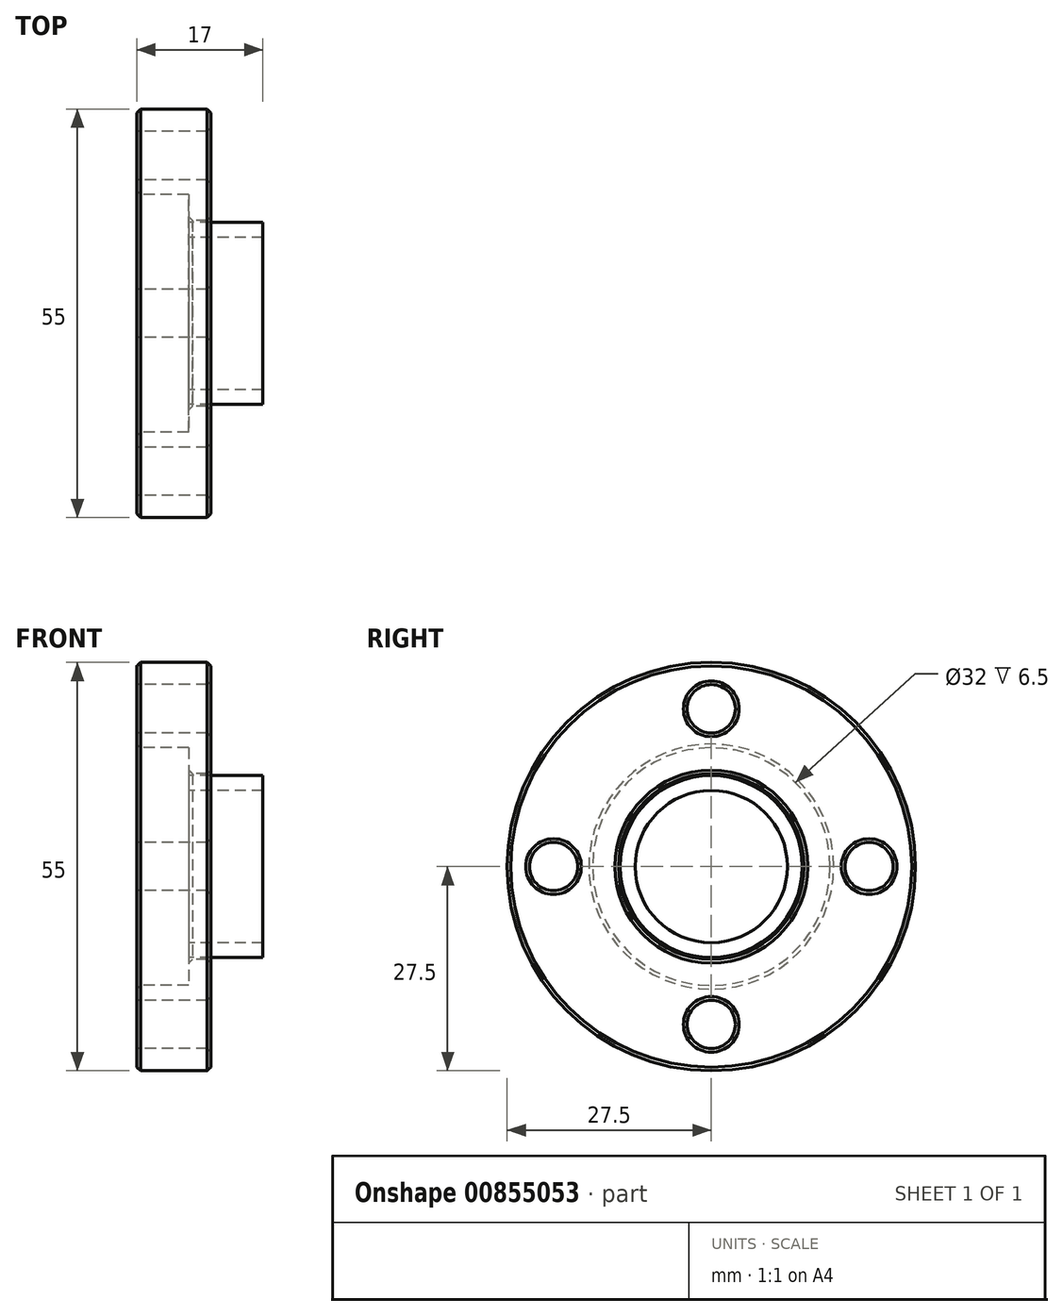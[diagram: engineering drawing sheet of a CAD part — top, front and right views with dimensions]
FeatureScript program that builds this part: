
annotation { "Feature Type Name" : "Feature", "Feature Type Description" : "" }
export const myFeature = defineFeature(function(context is Context, id is Id, definition is map)
    precondition{}
    {
        {
            var Q0;
            Q0=qCreatedBy(makeId("Front.planeOp"),FACE);
            var sketch = newSketch(context, id + "F0", { "sketchPlane" : qUnion([Q0])});
            skLineSegment(sketch, "E0", {"start": v(-73.36, 0) * mm, "end": v(72.8, 0) * mm, "construction": true});
            skLineSegment(sketch, "E1", {"start": v(0, 27.5) * mm, "end": v(10, 27.5) * mm});
            skLineSegment(sketch, "E2", {"start": v(10, 27.5) * mm, "end": v(10, 12.5) * mm});
            skLineSegment(sketch, "E3", {"start": v(10, 12.5) * mm, "end": v(7, 12.5) * mm});
            skLineSegment(sketch, "E4", {"start": v(7, 12.5) * mm, "end": v(7, 16) * mm});
            skLineSegment(sketch, "E5", {"start": v(7, 16) * mm, "end": v(0, 16) * mm});
            skLineSegment(sketch, "E6", {"start": v(0, 16) * mm, "end": v(0, 27.5) * mm});
            skSolve(sketch);
        }
        {
            var Q0;
            Q0 = qSketchRegion(id + "F0", true);
            var Q1;
            Q1=sQuery(id+"F0.wireOp",EDGE,"E0");
            revolve(context, id + "F1", {"surfaceOperationType" : NewSurfaceOperationType.NEW, "entities" : qUnion([Q0]), "axis" : qUnion([Q1]), "revolveType" : RevolveType.FULL});
        }
        {
            var Q0;
            Q0=makeQuery(id+"F1.opRevolve","SWEPT_FACE",FACE,{"disambiguationData":[OSD([sQuery(id+"F0.wireOp",EDGE,"E6")])]});
            var sketch = newSketch(context, id + "F2", { "sketchPlane" : qUnion([Q0])});
            skCircle(sketch, "E7", {"center": v(0, 0) * mm, "radius": 21.25 * mm, "construction": true});
            skCircle(sketch, "E8", {"center": v(0, -21.25) * mm, "radius": 3.25 * mm});
            skCircle(sketch, "E9", {"center": v(21.25, 0) * mm, "radius": 3.25 * mm});
            skCircle(sketch, "E10", {"center": v(0, 21.25) * mm, "radius": 3.25 * mm});
            skCircle(sketch, "E11", {"center": v(-21.25, 0) * mm, "radius": 3.25 * mm});
            skSolve(sketch);
        }
        {
            var Q0;
            Q0 = qSketchRegion(id + "F2", true);
            extrude(context, id + "F3", {"entities" : qUnion([Q0]), "operationType" : NewBodyOperationType.REMOVE, "endBound" : BoundingType.THROUGH_ALL, "oppositeDirection" : true, "depth" : 25 * mm, "offsetDistance" : 25 * mm});
        }
        {
            var Q0;
            Q0=makeQuery(id+"F1.opRevolve","SWEPT_EDGE",EDGE,{"disambiguationData":[OSD([sQuery(id+"F0.wireOp",EDGE,"E1"),sQuery(id+"F0.wireOp",EDGE,"E2")])]});
            var Q1;
            Q1=makeQuery(id+"F1.opRevolve","SWEPT_EDGE",EDGE,{"disambiguationData":[OSD([sQuery(id+"F0.wireOp",EDGE,"E2"),sQuery(id+"F0.wireOp",EDGE,"E3")])]});
            var Q2;
            Q2=makeQuery(id+"F1.opRevolve","SWEPT_EDGE",EDGE,{"disambiguationData":[OSD([sQuery(id+"F0.wireOp",EDGE,"E1"),sQuery(id+"F0.wireOp",EDGE,"E6")])]});
            var Q3;
            Q3=makeQuery(id+"F1.opRevolve","SWEPT_EDGE",EDGE,{"disambiguationData":[OSD([sQuery(id+"F0.wireOp",EDGE,"E5"),sQuery(id+"F0.wireOp",EDGE,"E6")])]});
            var Q4;
            Q4=makeQuery(id+"F1.opRevolve","SWEPT_EDGE",EDGE,{"disambiguationData":[OSD([sQuery(id+"F0.wireOp",EDGE,"E3"),sQuery(id+"F0.wireOp",EDGE,"E4")])]});
            var Q5;
            Q5=makeQuery(id+"F3.boolean.opBoolean","COPY",EDGE,{"derivedFrom":makeQuery(id+"F3.opExtrude","CAP_EDGE",EDGE,{"disambiguationData":[OSD([sQuery(id+"F2.wireOp",EDGE,"E9")])],"isStart":true})});
            var Q6;
            Q6=makeQuery(id+"F3.boolean.opBoolean","COPY",EDGE,{"derivedFrom":makeQuery(id+"F3.opExtrude","CAP_EDGE",EDGE,{"disambiguationData":[OSD([sQuery(id+"F2.wireOp",EDGE,"E8")])],"isStart":true})});
            var Q7;
            Q7=makeQuery(id+"F3.boolean.opBoolean","COPY",EDGE,{"derivedFrom":makeQuery(id+"F3.opExtrude","CAP_EDGE",EDGE,{"disambiguationData":[OSD([sQuery(id+"F2.wireOp",EDGE,"E11")])],"isStart":true})});
            var Q8;
            Q8=makeQuery(id+"F3.boolean.opBoolean","COPY",EDGE,{"derivedFrom":makeQuery(id+"F3.opExtrude","CAP_EDGE",EDGE,{"disambiguationData":[OSD([sQuery(id+"F2.wireOp",EDGE,"E10")])],"isStart":true})});
            var Q9;
            Q9=makeQuery(id+"F3.boolean.opBoolean","INTERSECT",EDGE,{"derivedFrom":[makeQuery(id+"F1.opRevolve","SWEPT_FACE",FACE,{"disambiguationData":[OSD([sQuery(id+"F0.wireOp",EDGE,"E2")])]}),makeQuery(id+"F3.opExtrude","SWEPT_FACE",FACE,{"disambiguationData":[OSD([sQuery(id+"F2.wireOp",EDGE,"E10")])]})]});
            var Q10;
            Q10=makeQuery(id+"F3.boolean.opBoolean","INTERSECT",EDGE,{"derivedFrom":[makeQuery(id+"F1.opRevolve","SWEPT_FACE",FACE,{"disambiguationData":[OSD([sQuery(id+"F0.wireOp",EDGE,"E2")])]}),makeQuery(id+"F3.opExtrude","SWEPT_FACE",FACE,{"disambiguationData":[OSD([sQuery(id+"F2.wireOp",EDGE,"E11")])]})]});
            var Q11;
            Q11=makeQuery(id+"F3.boolean.opBoolean","INTERSECT",EDGE,{"derivedFrom":[makeQuery(id+"F1.opRevolve","SWEPT_FACE",FACE,{"disambiguationData":[OSD([sQuery(id+"F0.wireOp",EDGE,"E2")])]}),makeQuery(id+"F3.opExtrude","SWEPT_FACE",FACE,{"disambiguationData":[OSD([sQuery(id+"F2.wireOp",EDGE,"E8")])]})]});
            var Q12;
            Q12=makeQuery(id+"F3.boolean.opBoolean","INTERSECT",EDGE,{"derivedFrom":[makeQuery(id+"F1.opRevolve","SWEPT_FACE",FACE,{"disambiguationData":[OSD([sQuery(id+"F0.wireOp",EDGE,"E2")])]}),makeQuery(id+"F3.opExtrude","SWEPT_FACE",FACE,{"disambiguationData":[OSD([sQuery(id+"F2.wireOp",EDGE,"E9")])]})]});
            chamfer(context, id + "F4", {"entities" : qUnion([Q0, Q1, Q2, Q3, Q4, Q5, Q6, Q7, Q8, Q9, Q10, Q11, Q12]), "width" : .5 * mm, "tangentPropagation" : true});
        }
        {
            var Q0;
            Q0=makeQuery(id+"F1.opRevolve","SWEPT_FACE",FACE,{"disambiguationData":[OSD([sQuery(id+"F0.wireOp",EDGE,"E4")])]});
            var sketch = newSketch(context, id + "F5", { "sketchPlane" : qUnion([Q0])});
            skCircle(sketch, "E12", {"center": v(0, 0) * mm, "radius": 12.25 * mm});
            skCircle(sketch, "E13", {"center": v(0, 0) * mm, "radius": 10.25 * mm});
            skSolve(sketch);
        }
        {
            var Q0;
            Q0 = qSketchRegion(id + "F5", true);
            extrude(context, id + "F6", {"entities" : qUnion([Q0]), "oppositeDirection" : true, "depth" : 10 * mm, "offsetDistance" : 25 * mm});
        }
    });
